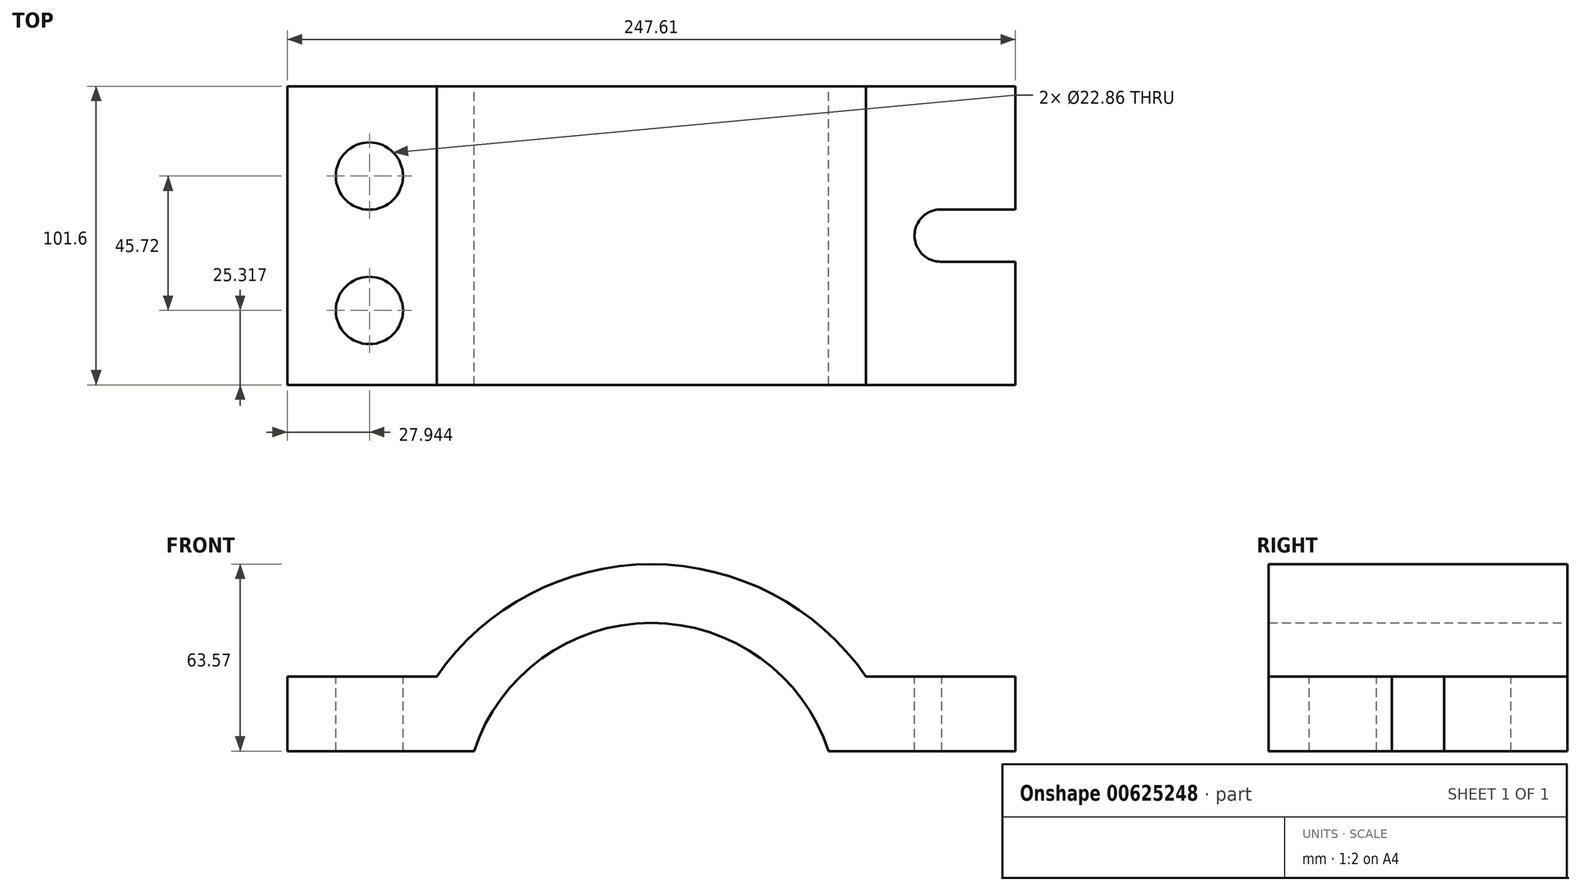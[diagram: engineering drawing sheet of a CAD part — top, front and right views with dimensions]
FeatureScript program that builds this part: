
annotation { "Feature Type Name" : "Feature", "Feature Type Description" : "" }
export const myFeature = defineFeature(function(context is Context, id is Id, definition is map)
    precondition{}
    {
        {
            var Q0;
            Q0=qCreatedBy(makeId("Front.planeOp"),FACE);
            var sketch = newSketch(context, id + "F0", { "sketchPlane" : qUnion([Q0])});
            skLineSegment(sketch, "E0", {"start": v(-143.27, -44.95) * mm, "end": v(-79.77, -44.95) * mm});
            skLineSegment(sketch, "E1", {"start": v(-143.27, -44.95) * mm, "end": v(-143.27, -19.55) * mm});
            skLineSegment(sketch, "E2", {"start": v(-143.27, -19.55) * mm, "end": v(-92.47, -19.55) * mm});
            skLineSegment(sketch, "E3", {"start": v(104.34, -44.95) * mm, "end": v(104.34, -19.55) * mm});
            skLineSegment(sketch, "E4", {"start": v(104.34, -19.55) * mm, "end": v(53.54, -19.55) * mm});
            skArc(sketch, "E5", {"start": v(53.54, -19.55) * mm, "mid": v(-19.46, 18.62) * mm, "end": v(-92.47, -19.55) * mm});
            skPoint(sketch, "E6", {"position": v(-79.77, -44.95) * mm});
            skPoint(sketch, "E7", {"position": v(40.84, -44.95) * mm});
            skLineSegment(sketch, "E8.trimOffspring", {"start": v(40.84, -44.95) * mm, "end": v(104.34, -44.95) * mm});
            skArc(sketch, "E9", {"start": v(40.84, -44.95) * mm, "mid": v(-19.46, -1.35) * mm, "end": v(-79.77, -44.95) * mm});
            skPoint(sketch, "E10", {"position": v(-143.27, -44.95) * mm});
            skPoint(sketch, "E11", {"position": v(104.34, -44.95) * mm});
            skSolve(sketch);
        }
        {
            var Q0;
            Q0 = qSketchRegion(id + "F0", true);
            extrude(context, id + "F1", {"entities" : qUnion([Q0]), "endBound" : BoundingType.SYMMETRIC, "depth" : 101.6 * mm, "offsetDistance" : 25.4 * mm});
        }
        {
            var Q0;
            Q0=makeQuery(id+"F1.opExtrude","SWEPT_FACE",FACE,{"disambiguationData":[OSD([sQuery(id+"F0.wireOp",EDGE,"E2")])]});
            var sketch = newSketch(context, id + "F2", { "sketchPlane" : qUnion([Q0])});
            skCircle(sketch, "E12", {"center": v(-115.33, 20.24) * mm, "radius": 11.43 * mm});
            skCircle(sketch, "E13", {"center": v(-115.33, -25.48) * mm, "radius": 11.43 * mm});
            skSolve(sketch);
        }
        {
            var Q0;
            Q0=sQuery(id+"F2.wireOp",VERTEX,"E12.center");
            var Q1;
            Q1=sQuery(id+"F2.wireOp",VERTEX,"E13.center");
            var Q2;
            Q2=makeQuery(id+"F1.opExtrude","SWEPT_BODY",BODY,{"disambiguationData":[OSD([sQuery(id+"F0.wireOp",EDGE,"E0"),sQuery(id+"F0.wireOp",EDGE,"E1"),sQuery(id+"F0.wireOp",EDGE,"E2"),sQuery(id+"F0.wireOp",EDGE,"E3"),sQuery(id+"F0.wireOp",EDGE,"E4"),sQuery(id+"F0.wireOp",EDGE,"E5"),sQuery(id+"F0.wireOp",EDGE,"E8.trimOffspring"),sQuery(id+"F0.wireOp",EDGE,"E9")])]});
            hole(context, id + "F3", {"style" : HoleStyle.SIMPLE, "endStyle" : HoleEndStyle.THROUGH, "holeDiameter" : 22.86 * mm, "majorDiameter" : 6.35 * mm, "isTappedThrough" : true, "tappedDepth" : 12.7 * mm, "tapClearance" : 3, "locations" : qUnion([Q0, Q1]), "scope" : qUnion([Q2])});
        }
        {
            var Q0;
            Q0=qCreatedBy(makeId("Top.planeOp"),FACE);
            var sketch = newSketch(context, id + "F4", { "sketchPlane" : qUnion([Q0])});
            skCircle(sketch, "E14", {"center": v(78.94, 0) * mm, "radius": 8.33 * mm});
            skSolve(sketch);
        }
        {
            var Q0;
            Q0=sQuery(id+"F4.wireOp",VERTEX,"E14.center");
            var Q1;
            Q1=makeQuery(id+"F1.opExtrude","SWEPT_BODY",BODY,{"disambiguationData":[OSD([sQuery(id+"F0.wireOp",EDGE,"E0"),sQuery(id+"F0.wireOp",EDGE,"E1"),sQuery(id+"F0.wireOp",EDGE,"E2"),sQuery(id+"F0.wireOp",EDGE,"E3"),sQuery(id+"F0.wireOp",EDGE,"E4"),sQuery(id+"F0.wireOp",EDGE,"E5"),sQuery(id+"F0.wireOp",EDGE,"E8.trimOffspring"),sQuery(id+"F0.wireOp",EDGE,"E9")])]});
            hole(context, id + "F5", {"style" : HoleStyle.SIMPLE, "endStyle" : HoleEndStyle.THROUGH, "holeDiameter" : 17.78 * mm, "majorDiameter" : 6.35 * mm, "isTappedThrough" : true, "tappedDepth" : 12.7 * mm, "tapClearance" : 3, "locations" : qUnion([Q0]), "scope" : qUnion([Q1])});
        }
        {
            var Q0;
            Q0=makeQuery(id+"F1.opExtrude","SWEPT_FACE",FACE,{"disambiguationData":[OSD([sQuery(id+"F0.wireOp",EDGE,"E4")])]});
            var sketch = newSketch(context, id + "F6", { "sketchPlane" : qUnion([Q0])});
            skLineSegment(sketch, "E15", {"start": v(79.34, -8.88) * mm, "end": v(104.34, -8.88) * mm});
            skLineSegment(sketch, "E16", {"start": v(78.97, 8.89) * mm, "end": v(104.34, 8.89) * mm});
            skLineSegment(sketch, "E17", {"start": v(104.34, 8.89) * mm, "end": v(104.34, -8.88) * mm});
            skSolve(sketch);
        }
        {
            var Q0;
            {var subQ0=sQuery(id+"F6.wireOp",EDGE,"E15");Q0=makeQuery(id+"F6.imprint","IMPRINT",FACE,{"disambiguationData":[TD([[makeQuery(id+"F6.imprint","IMPRINT",EDGE,{"derivedFrom":subQ0}),1.0]])]});}
            extrude(context, id + "F7", {"entities" : qUnion([Q0]), "operationType" : NewBodyOperationType.REMOVE, "oppositeDirection" : true, "depth" : 25.4 * mm, "offsetDistance" : 25.4 * mm});
        }
    });
